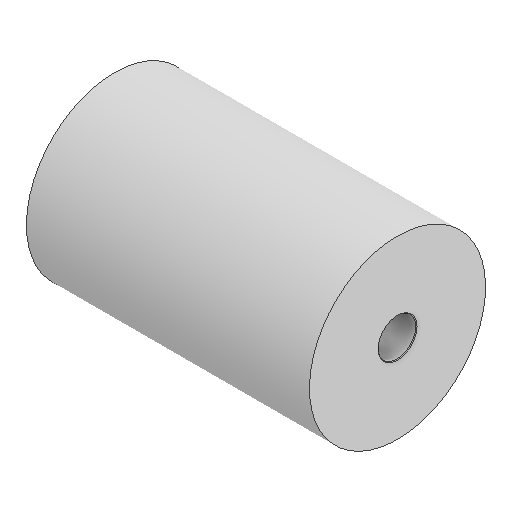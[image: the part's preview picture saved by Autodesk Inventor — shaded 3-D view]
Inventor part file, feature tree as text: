
AUTODESK INVENTOR PART (.ipt)
format: ipt  version: 2022 (Build 260153000, 153)  size: 112,128 bytes
history: native  units: mm
features: sketch x2, other x1, extrude x1, hole x1, fillet x1
ambient origin geometry x8: Origin, YZ Plane, XZ Plane, XY Plane, X Axis, Y Axis, Z Axis, Center Point
bodies: Body1 (feature_tree)
feature tree (6):
  other  "Твердое тело1"
  extrude  "Выдавливание1"  Depth=45.0mm TaperAngle=0.0deg
  hole  "Отверстие1"  [1 undecoded]
  fillet  "Сопряжение1"  [1 undecoded]
  sketch  "Эскиз1"
  sketch  "Эскиз2"
note: 2 required parameter values undecoded (feature->parameter linkage not recoverable at this tier; creation-order binding heuristic only, values carry confidence <= 0.55)
